# Revit family: RPC Tree - Fall
name_source: partatom
category: Planting
revit_build: Autodesk Revit Architecture 2012 (Build: 20110210_1515)
units: mm (PartAtom-declared; Revit-internal decimal feet)

## types (16) — shared parameters
Assembly Code = G2050500

## per-type parameters (varying)
| type | Height | Type Comments |
| American Beech - 20' | 20' - 0" | American Beech |
| Black Oak - 60' | 60' - 0" | Black Oak |
| Dogwood - 30' | 30' - 0" | Dogwood |
| Elm (Sapling) - 10' | 10' - 0" | Elm (Sapling) |
| Gray Birch - 10' | 10' - 0" | Gray Birch |
| Honey Locust - 25' | 25' - 0" | Honey Locust |
| Japanese Maple - 10' | 10' - 0" | Japanese Maple |
| Lombardy Poplar - 40' | 40' - 0" | Lombardy Poplar |
| Red Ash - 25' | 25' - 0" | Red Ash |
| Red Oak - 62' | 62' - 0" | Red Oak |
| Scarlet Oak - 42' | 42' - 0" | Scarlet Oak |
| Service Berry - 25' | 25' - 0" | Service Berry |
| Shumard Oak - 40' | 40' - 0" | Shumard Oak |
| Sugar Maple - 45' | 45' - 0" | Sugar Maple |
| Sycamore - 58' | 58' - 0" | Sycamore |
| White Ash - 30' | 30' - 0" | White Ash |

## geometry (parser evidence)
native form markers: Sweep x1
no freeform markers — native parametric forms only
